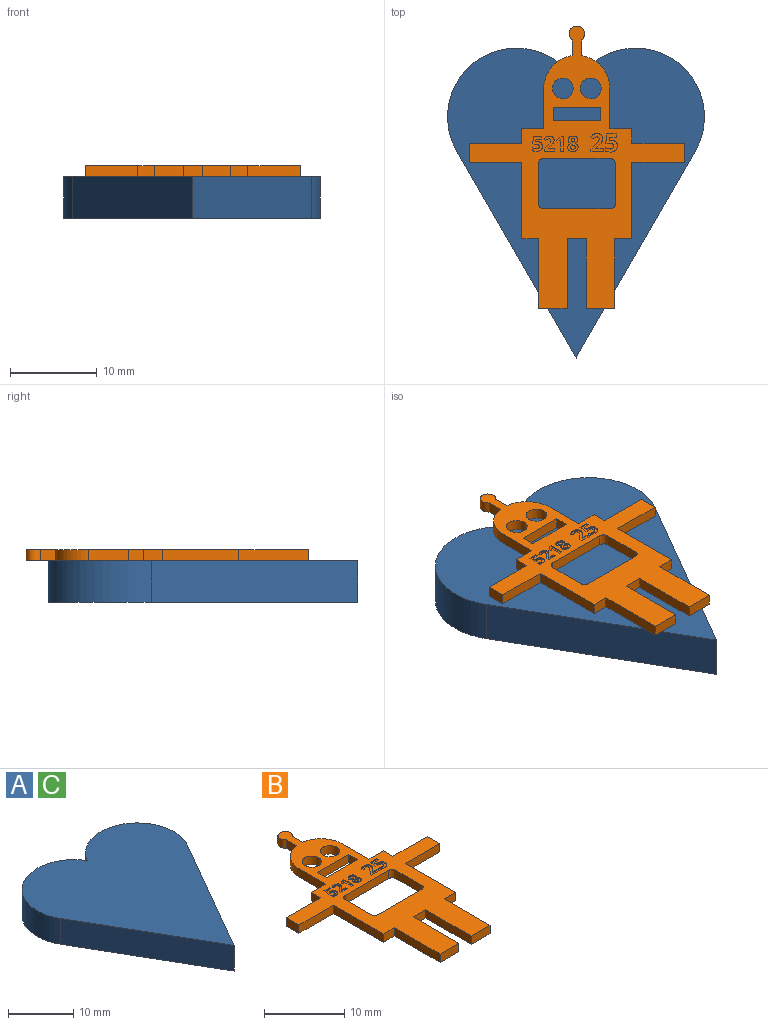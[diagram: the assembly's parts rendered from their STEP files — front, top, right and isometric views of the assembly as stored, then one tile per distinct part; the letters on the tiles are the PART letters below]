
ASSEMBLY  parts=3 mates=1
PART A: 6 faces, bbox 29.6x35.7x4.8 mm
  f0: plane 23.82x13.75mm, normal (-0.87,-0.5,0), area 132.7mm2, adj f1,f3,f4,f5
  f1: plane 23.82x13.75mm, normal (0.87,-0.5,0), area 132.7mm2, adj f0,f2,f4,f5
  f2: cylinder r=7.94mm len=14.82mm, axis (0,0,-1), area 120.4mm2, adj f1,f3,f4,f5
  f3: cylinder r=7.94mm len=14.82mm, axis (0,0,-1), area 120.4mm2, adj f0,f2,f4,f5
  f4: plane 35.73x29.63mm, normal (0,0,1), area 634.9mm2, adj f0,f1,f2,f3
  f5: plane 35.73x29.63mm, normal (0,0,-1), area 634.9mm2, adj f0,f1,f2,f3
PART B: 181 faces, bbox 24.8x32.6x1.3 mm
  f0: plane 32.6x24.81mm, normal (0,0,1), area 226.5mm2, adj f2,f3,f4,f5,f6,f7,f8,f9
  f1: plane 32.6x24.81mm, normal (0,0,-1), area 234.3mm2, adj f2,f3,f4,f5,f6,f7,f8,f9
  f2: plane 2.54x1.27mm, normal (0,1,0), area 3.2mm2, adj f0,f1,f3,f29
  f3: plane 4.64x1.27mm, normal (1,0,0), area 5.9mm2, adj f0,f1,f2,f4
  f4: cylinder r=3.81mm len=3.77mm, axis (0,0,-1), area 6.9mm2, adj f0,f1,f3,f5
  f5: plane 1.81x1.27mm, normal (1,0,0), area 2.3mm2, adj f0,f1,f4,f6
  f6: cylinder r=0.9mm len=1.8mm, axis (0,0,-1), area 5.7mm2, adj f0,f1,f5,f7
  f7: plane 1.81x1.27mm, normal (-1,0,0), area 2.3mm2, adj f0,f1,f6,f8
  f8: cylinder r=3.81mm len=3.77mm, axis (0,0,-1), area 6.9mm2, adj f0,f1,f7,f9
  f9: plane 4.64x1.27mm, normal (-1,0,0), area 5.9mm2, adj f0,f1,f8,f10
  f10: plane 2.54x1.27mm, normal (0,1,0), area 3.2mm2, adj f0,f1,f9,f11
  f11: plane 1.68x1.27mm, normal (-1,0,0), area 2.1mm2, adj f0,f1,f10,f12
  f12: plane 6.06x1.27mm, normal (0,1,0), area 7.7mm2, adj f0,f1,f11,f13
  f13: plane 2.21x1.27mm, normal (-1,0,0), area 2.8mm2, adj f0,f1,f12,f14
  f14: plane 6.06x1.27mm, normal (0,-1,0), area 7.7mm2, adj f0,f1,f13,f15
  f15: plane 8.81x1.27mm, normal (-1,0,0), area 11.2mm2, adj f0,f1,f14,f16
  f16: plane 1.94x1.27mm, normal (0,-1,0), area 2.5mm2, adj f0,f1,f15,f17
  f17: plane 8.06x1.27mm, normal (-1,0,0), area 10.2mm2, adj f0,f1,f16,f18
  f18: plane 3.29x1.27mm, normal (0,-1,0), area 4.2mm2, adj f0,f1,f17,f19
  f19: plane 8.06x1.27mm, normal (1,0,0), area 10.2mm2, adj f0,f1,f18,f20
  f20: plane 2.2x1.27mm, normal (0,-1,0), area 2.8mm2, adj f0,f1,f19,f21
  f21: plane 8.06x1.27mm, normal (-1,0,0), area 10.2mm2, adj f0,f1,f20,f22
  f22: plane 3.29x1.27mm, normal (0,-1,0), area 4.2mm2, adj f0,f1,f21,f23
  f23: plane 8.06x1.27mm, normal (1,0,0), area 10.2mm2, adj f0,f1,f22,f24
  f24: plane 1.98x1.27mm, normal (0,-1,0), area 2.5mm2, adj f0,f1,f23,f25
  f25: plane 8.81x1.27mm, normal (1,0,0), area 11.2mm2, adj f0,f1,f24,f26
  f26: plane 6.06x1.27mm, normal (0,-1,0), area 7.7mm2, adj f0,f1,f25,f27
  f27: plane 2.21x1.27mm, normal (1,0,0), area 2.8mm2, adj f0,f1,f26,f28
  f28: plane 6.06x1.27mm, normal (0,1,0), area 7.7mm2, adj f0,f1,f27,f29
  f29: plane 1.68x1.27mm, normal (1,0,0), area 2.1mm2, adj f0,f1,f2,f28
  f30: cylinder r=1.19mm len=2.39mm, axis (0,0,1), area 9.5mm2, adj f0,f1
  f31: cylinder r=1.19mm len=2.39mm, axis (0,0,1), area 9.5mm2, adj f0,f1
  f32: plane 5.49x1.27mm, normal (0,1,0), area 7mm2, adj f0,f1,f33,f35
  f33: plane 1.58x1.27mm, normal (-1,0,0), area 2mm2, adj f0,f1,f32,f34
  f34: plane 5.49x1.27mm, normal (0,-1,0), area 7mm2, adj f0,f1,f33,f35
  f35: plane 1.58x1.27mm, normal (1,0,0), area 2mm2, adj f0,f1,f32,f34
  f36: plane 4.55x1.27mm, normal (-1,0,0), area 5.8mm2, adj f0,f1,f40,f43
  f37: plane 7.67x1.27mm, normal (0,-1,0), area 9.7mm2, adj f0,f1,f42,f43
  f38: plane 4.55x1.27mm, normal (1,0,0), area 5.8mm2, adj f0,f1,f41,f42
  f39: plane 7.67x1.27mm, normal (0,1,0), area 9.7mm2, adj f0,f1,f40,f41
  f40: cylinder r=0.64mm len=1.27mm, axis (0,0,-1), area 1.3mm2, adj f0,f1,f36,f39
  f41: cylinder r=0.64mm len=1.27mm, axis (0,0,1), area 1.3mm2, adj f0,f1,f38,f39
  f42: cylinder r=0.64mm len=1.27mm, axis (0,0,-1), area 1.3mm2, adj f0,f1,f37,f38
  f43: cylinder r=0.64mm len=1.27mm, axis (0,0,1), area 1.3mm2, adj f0,f1,f36,f37
  f44: plane 1.44x0.13mm, normal (0,1,0), area 0.2mm2, adj f0,f45,f67,f68
  f45: plane 0.37x0.13mm, normal (-1,0,0), area 0mm2, adj f0,f44,f46,f68
  f46: plane 0.9x0.13mm, normal (0,-1,0), area 0.1mm2, adj f0,f45,f47,f68
  f47: plane 0.13x0.02mm, normal (-1,0,0), area 0mm2, adj f0,f46,f48,f68
  f48: plane 0.26x0.25mm, normal (-0.69,0.73,0), area 0mm2, adj f0,f47,f49,f68
  f49: extruded ~0.37x0.37mm, area 0.1mm2, adj f0,f48,f50,f68
  f50: extruded ~0.26x0.15mm, area 0mm2, adj f0,f49,f51,f68
  f51: extruded ~0.27x0.13mm, area 0mm2, adj f0,f50,f52,f68
  f52: extruded ~0.29x0.13mm, area 0mm2, adj f0,f51,f53,f68
  f53: extruded ~0.23x0.2mm, area 0mm2, adj f0,f52,f54,f68
  f54: extruded ~0.34x0.13mm, area 0mm2, adj f0,f53,f55,f68
  f55: extruded ~0.26x0.13mm, area 0mm2, adj f0,f54,f56,f68
  f56: extruded ~0.22x0.13mm, area 0mm2, adj f0,f55,f57,f68
  f57: extruded ~0.25x0.18mm, area 0mm2, adj f0,f56,f58,f68
  f58: plane 0.28x0.24mm, normal (0.76,0.65,0), area 0mm2, adj f0,f57,f59,f68
  f59: extruded ~0.24x0.16mm, area 0mm2, adj f0,f58,f60,f68
  f60: extruded ~0.23x0.13mm, area 0mm2, adj f0,f59,f61,f68
  f61: extruded ~0.18x0.13mm, area 0mm2, adj f0,f60,f62,f68
  f62: extruded ~0.18x0.13mm, area 0mm2, adj f0,f61,f63,f68
  f63: extruded ~0.16x0.13mm, area 0mm2, adj f0,f62,f64,f68
  f64: extruded ~0.17x0.13mm, area 0mm2, adj f0,f63,f65,f68
  f65: extruded ~0.33x0.3mm, area 0.1mm2, adj f0,f64,f66,f68
  f66: plane 0.52x0.52mm, normal (0.71,-0.7,0), area 0.1mm2, adj f0,f65,f67,f68
  f67: plane 0.3x0.13mm, normal (1,0,0), area 0mm2, adj f0,f44,f66,f68
  f68: plane 2.08x1.44mm, normal (0,0,1), area 1.6mm2, adj f44,f45,f46,f47,f48,f49,f50,f51
  f69: extruded ~0.47x0.17mm, area 0.1mm2, adj f0,f70,f88,f89
  f70: extruded ~0.21x0.13mm, area 0mm2, adj f0,f69,f71,f89
  f71: plane 0.13x0.05mm, normal (0.2,-0.98,0), area 0mm2, adj f0,f70,f72,f89
  f72: plane 0.4x0.13mm, normal (-1,0.09,0), area 0.1mm2, adj f0,f71,f73,f89
  f73: plane 0.73x0.13mm, normal (0,1,0), area 0.1mm2, adj f0,f72,f74,f89
  f74: plane 0.37x0.13mm, normal (-1,0,0), area 0mm2, adj f0,f73,f75,f89
  f75: plane 1.11x0.13mm, normal (0,-1,0), area 0.1mm2, adj f0,f74,f76,f89
  f76: plane 1.05x0.13mm, normal (1,-0.07,0), area 0.1mm2, adj f0,f75,f77,f89
  f77: plane 0.17x0.13mm, normal (0.47,0.88,0), area 0mm2, adj f0,f76,f78,f89
  f78: extruded ~0.15x0.13mm, area 0mm2, adj f0,f77,f79,f89
  f79: extruded ~0.16x0.13mm, area 0mm2, adj f0,f78,f80,f89
  f80: extruded ~0.41x0.31mm, area 0.1mm2, adj f0,f79,f81,f89
  f81: extruded ~0.4x0.33mm, area 0.1mm2, adj f0,f80,f82,f89
  f82: extruded ~0.28x0.13mm, area 0mm2, adj f0,f81,f83,f89
  f83: extruded ~0.26x0.13mm, area 0mm2, adj f0,f82,f84,f89
  f84: plane 0.38x0.13mm, normal (1,0,0), area 0mm2, adj f0,f83,f85,f89
  f85: extruded ~0.55x0.13mm, area 0.1mm2, adj f0,f84,f86,f89
  f86: extruded ~0.61x0.19mm, area 0.1mm2, adj f0,f85,f87,f89
  f87: extruded ~0.53x0.21mm, area 0.1mm2, adj f0,f86,f88,f89
  f88: extruded ~0.46x0.18mm, area 0.1mm2, adj f0,f69,f87,f89
  f89: plane 2.08x1.37mm, normal (0,0,1), area 1.7mm2, adj f69,f70,f71,f72,f73,f74,f75,f76
  f90: extruded ~0.15x0.13mm, area 0mm2, adj f91,f120,f121,f180
  f91: extruded ~0.15x0.13mm, area 0mm2, adj f90,f92,f121,f180
  f92: extruded ~0.13x0.13mm, area 0mm2, adj f91,f93,f121,f180
  f93: extruded ~0.13x0.13mm, area 0mm2, adj f92,f94,f121,f180
  f94: extruded ~0.16x0.13mm, area 0mm2, adj f93,f95,f121,f180
  f95: extruded ~0.16x0.13mm, area 0mm2, adj f94,f96,f121,f180
  f96: extruded ~0.13x0.13mm, area 0mm2, adj f95,f120,f121,f180
  f97: extruded ~0.16x0.13mm, area 0mm2, adj f98,f118,f121,f122
  f98: extruded ~0.29x0.25mm, area 0.1mm2, adj f97,f99,f121,f122
  f99: extruded ~0.21x0.15mm, area 0mm2, adj f98,f100,f121,f122
  f100: extruded ~0.15x0.13mm, area 0mm2, adj f99,f101,f121,f122
  f101: extruded ~0.15x0.13mm, area 0mm2, adj f100,f102,f121,f122
  f102: extruded ~0.2x0.13mm, area 0mm2, adj f101,f118,f121,f122
  f103: extruded ~0.4x0.13mm, area 0.1mm2, adj f0,f104,f119,f121
  f104: extruded ~0.4x0.13mm, area 0.1mm2, adj f0,f103,f105,f121
  f105: extruded ~0.3x0.15mm, area 0mm2, adj f0,f104,f106,f121
  f106: extruded ~0.23x0.13mm, area 0mm2, adj f0,f105,f107,f121
  f107: extruded ~0.21x0.2mm, area 0mm2, adj f0,f106,f108,f121
  f108: extruded ~0.25x0.2mm, area 0mm2, adj f0,f107,f109,f121
  f109: extruded ~0.26x0.13mm, area 0mm2, adj f0,f108,f110,f121
  f110: extruded ~0.34x0.16mm, area 0mm2, adj f0,f109,f111,f121
  f111: extruded ~0.44x0.13mm, area 0.1mm2, adj f0,f110,f112,f121
  f112: extruded ~0.43x0.13mm, area 0.1mm2, adj f0,f111,f113,f121
  f113: extruded ~0.34x0.16mm, area 0mm2, adj f0,f112,f114,f121
  f114: extruded ~0.25x0.13mm, area 0mm2, adj f0,f113,f115,f121
  f115: extruded ~0.28x0.21mm, area 0mm2, adj f0,f114,f116,f121
  f116: extruded ~0.23x0.18mm, area 0mm2, adj f0,f115,f117,f121
  f117: extruded ~0.23x0.13mm, area 0mm2, adj f0,f116,f119,f121
  f118: extruded ~0.19x0.13mm, area 0mm2, adj f97,f102,f121,f122
  f119: extruded ~0.3x0.15mm, area 0mm2, adj f0,f103,f117,f121
  f120: extruded ~0.13x0.13mm, area 0mm2, adj f90,f96,f121,f180
  f121: plane 1.75x1.2mm, normal (0,0,1), area 1.3mm2, adj f90,f91,f92,f93,f94,f95,f96,f97
  f122: plane 0.53x0.5mm, normal (0,0,1), area 0.2mm2, adj f97,f98,f99,f100,f101,f102,f118
  f123: plane 0.36x0.13mm, normal (0,1,0), area 0mm2, adj f0,f124,f132,f133
  f124: plane 1.71x0.13mm, normal (-1,0,0), area 0.2mm2, adj f0,f123,f125,f133
  f125: plane 0.3x0.13mm, normal (0,-1,0), area 0mm2, adj f0,f124,f126,f133
  f126: plane 0.55x0.44mm, normal (0.62,-0.78,0), area 0.1mm2, adj f0,f125,f127,f133
  f127: plane 0.22x0.17mm, normal (0.78,0.63,0), area 0mm2, adj f0,f126,f128,f133
  f128: plane 0.2x0.16mm, normal (-0.63,0.78,0), area 0mm2, adj f0,f127,f129,f133
  f129: extruded ~0.13x0.13mm, area 0mm2, adj f0,f128,f130,f133
  f130: plane 0.18x0.13mm, normal (1,-0.03,0), area 0mm2, adj f0,f129,f131,f133
  f131: plane 0.16x0.13mm, normal (1,-0.02,0), area 0mm2, adj f0,f130,f132,f133
  f132: plane 0.99x0.13mm, normal (1,0,0), area 0.1mm2, adj f0,f123,f131,f133
  f133: plane 1.71x0.85mm, normal (0,0,1), area 0.8mm2, adj f123,f124,f125,f126,f127,f128,f129,f130
  f134: plane 1.19x0.13mm, normal (0,1,0), area 0.2mm2, adj f0,f135,f157,f158
  f135: plane 0.3x0.13mm, normal (-1,0,0), area 0mm2, adj f0,f134,f136,f158
  f136: plane 0.74x0.13mm, normal (0,-1,0), area 0.1mm2, adj f0,f135,f137,f158
  f137: plane 0.13x0.02mm, normal (-1,0,0), area 0mm2, adj f0,f136,f138,f158
  f138: plane 0.22x0.21mm, normal (-0.69,0.73,0), area 0mm2, adj f0,f137,f139,f158
  f139: extruded ~0.31x0.31mm, area 0.1mm2, adj f0,f138,f140,f158
  f140: extruded ~0.21x0.13mm, area 0mm2, adj f0,f139,f141,f158
  f141: extruded ~0.22x0.13mm, area 0mm2, adj f0,f140,f142,f158
  f142: extruded ~0.24x0.13mm, area 0mm2, adj f0,f141,f143,f158
  f143: extruded ~0.19x0.16mm, area 0mm2, adj f0,f142,f144,f158
  f144: extruded ~0.28x0.13mm, area 0mm2, adj f0,f143,f145,f158
  f145: extruded ~0.22x0.13mm, area 0mm2, adj f0,f144,f146,f158
  f146: extruded ~0.18x0.13mm, area 0mm2, adj f0,f145,f147,f158
  f147: extruded ~0.21x0.15mm, area 0mm2, adj f0,f146,f148,f158
  f148: plane 0.23x0.2mm, normal (0.76,0.65,0), area 0mm2, adj f0,f147,f149,f158
  f149: extruded ~0.2x0.13mm, area 0mm2, adj f0,f148,f150,f158
  f150: extruded ~0.19x0.13mm, area 0mm2, adj f0,f149,f151,f158
  f151: extruded ~0.15x0.13mm, area 0mm2, adj f0,f150,f152,f158
  f152: extruded ~0.15x0.13mm, area 0mm2, adj f0,f151,f153,f158
  f153: extruded ~0.13x0.13mm, area 0mm2, adj f0,f152,f154,f158
  f154: extruded ~0.14x0.13mm, area 0mm2, adj f0,f153,f155,f158
  f155: extruded ~0.27x0.25mm, area 0mm2, adj f0,f154,f156,f158
  f156: plane 0.43x0.43mm, normal (0.71,-0.7,0), area 0.1mm2, adj f0,f155,f157,f158
  f157: plane 0.25x0.13mm, normal (1,0,0), area 0mm2, adj f0,f134,f156,f158
  f158: plane 1.73x1.2mm, normal (0,0,1), area 1.1mm2, adj f134,f135,f136,f137,f138,f139,f140,f141
  f159: extruded ~0.39x0.14mm, area 0.1mm2, adj f0,f160,f178,f179
  f160: extruded ~0.18x0.13mm, area 0mm2, adj f0,f159,f161,f179
  f161: plane 0.13x0.04mm, normal (0.2,-0.98,0), area 0mm2, adj f0,f160,f162,f179
  f162: plane 0.34x0.13mm, normal (-1,0.09,0), area 0mm2, adj f0,f161,f163,f179
  f163: plane 0.61x0.13mm, normal (0,1,0), area 0.1mm2, adj f0,f162,f164,f179
  f164: plane 0.31x0.13mm, normal (-1,0,0), area 0mm2, adj f0,f163,f165,f179
  f165: plane 0.93x0.13mm, normal (0,-1,0), area 0.1mm2, adj f0,f164,f166,f179
  f166: plane 0.87x0.13mm, normal (1,-0.07,0), area 0.1mm2, adj f0,f165,f167,f179
  f167: plane 0.14x0.13mm, normal (0.47,0.88,0), area 0mm2, adj f0,f166,f168,f179
  f168: extruded ~0.13x0.12mm, area 0mm2, adj f0,f167,f169,f179
  f169: extruded ~0.14x0.13mm, area 0mm2, adj f0,f168,f170,f179
  f170: extruded ~0.34x0.26mm, area 0.1mm2, adj f0,f169,f171,f179
  f171: extruded ~0.33x0.27mm, area 0.1mm2, adj f0,f170,f172,f179
  f172: extruded ~0.23x0.13mm, area 0mm2, adj f0,f171,f173,f179
  f173: extruded ~0.21x0.13mm, area 0mm2, adj f0,f172,f174,f179
  f174: plane 0.31x0.13mm, normal (1,0,0), area 0mm2, adj f0,f173,f175,f179
  f175: extruded ~0.46x0.13mm, area 0.1mm2, adj f0,f174,f176,f179
  f176: extruded ~0.5x0.15mm, area 0.1mm2, adj f0,f175,f177,f179
  f177: extruded ~0.44x0.18mm, area 0.1mm2, adj f0,f176,f178,f179
  f178: extruded ~0.38x0.15mm, area 0.1mm2, adj f0,f159,f177,f179
  f179: plane 1.73x1.14mm, normal (0,0,1), area 1.2mm2, adj f159,f160,f161,f162,f163,f164,f165,f166
  f180: plane 0.41x0.41mm, normal (0,0,1), area 0.1mm2, adj f90,f91,f92,f93,f94,f95,f96,f120
PART C: same geometry as A
PLACE A at identity
PLACE B t=(0.1,8.18,4.83)mm
PLACE C at identity
MATE planar B.f1 <-> C.f4  axis (0,0,-1) through (-4.32,1.83,4.83)mm
